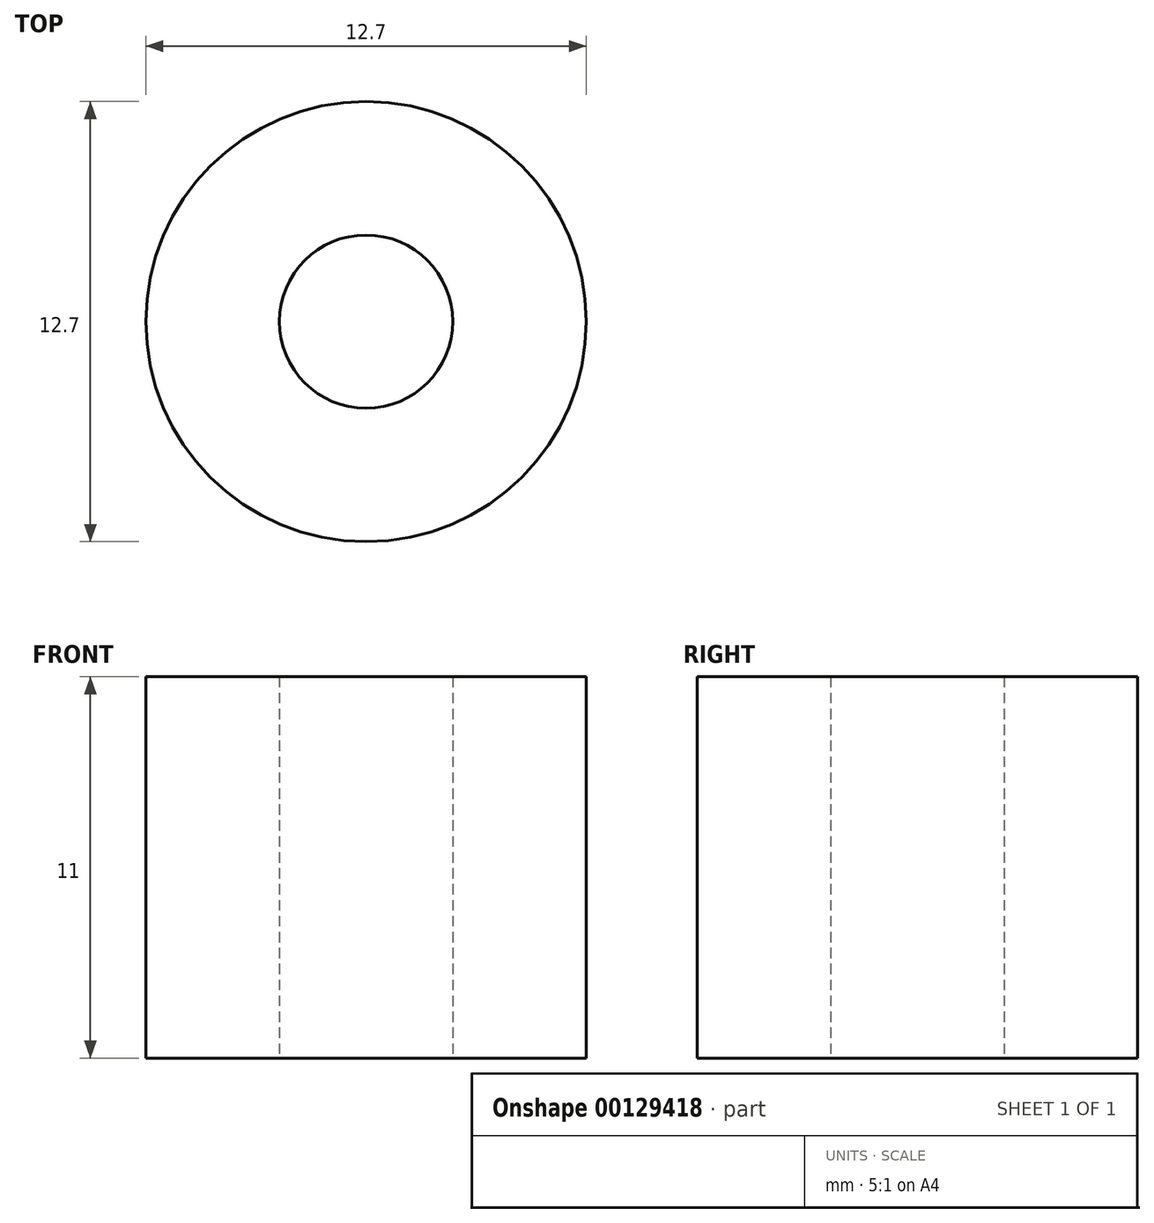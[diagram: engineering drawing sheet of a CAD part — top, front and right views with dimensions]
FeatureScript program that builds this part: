
annotation { "Feature Type Name" : "Feature", "Feature Type Description" : "" }
export const myFeature = defineFeature(function(context is Context, id is Id, definition is map)
    precondition{}
    {
        {
            var Q0;
            Q0=qCreatedBy(makeId("Top.planeOp"),FACE);
            var sketch = newSketch(context, id + "F0", { "sketchPlane" : qUnion([Q0])});
            skCircle(sketch, "E0", {"center": v(0, 0) * mm, "radius": 6.35 * mm});
            skCircle(sketch, "E1", {"center": v(0, 0) * mm, "radius": 2.5 * mm});
            skSolve(sketch);
        }
        {
            var Q0;
            Q0=qSketchRegion(id+"F0",true);
            extrude(context, id + "F1", {"entities" : qUnion([Q0]), "depth" : 11 * mm});
        }
    });
